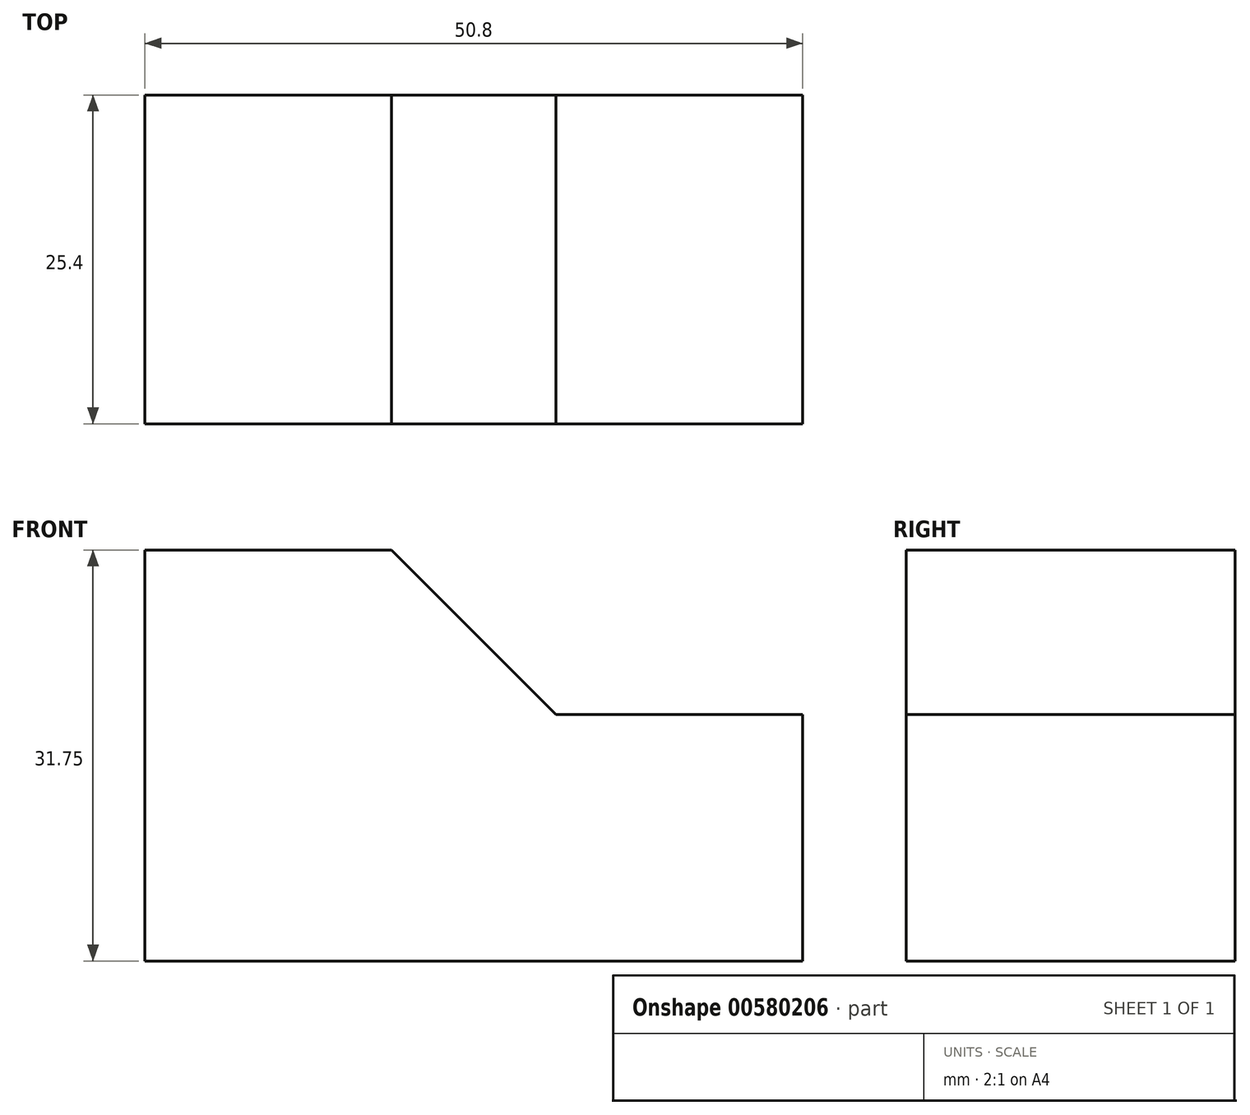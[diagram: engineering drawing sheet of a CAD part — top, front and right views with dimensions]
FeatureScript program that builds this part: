
annotation { "Feature Type Name" : "Feature", "Feature Type Description" : "" }
export const myFeature = defineFeature(function(context is Context, id is Id, definition is map)
    precondition{}
    {
        {
            var Q0;
            Q0=qCreatedBy(makeId("Front.planeOp"),FACE);
            var sketch = newSketch(context, id + "F0", { "sketchPlane" : qUnion([Q0])});
            skLineSegment(sketch, "E0", {"start": v(0, 0) * mm, "end": v(0, 31.75) * mm});
            skLineSegment(sketch, "E1", {"start": v(0, 31.75) * mm, "end": v(19.05, 31.75) * mm});
            skLineSegment(sketch, "E2", {"start": v(19.05, 31.75) * mm, "end": v(50.8, 0) * mm});
            skLineSegment(sketch, "E3", {"start": v(0, 0) * mm, "end": v(50.8, 0) * mm});
            skLineSegment(sketch, "E4", {"start": v(50.8, 0) * mm, "end": v(31.75, 19.05) * mm});
            skLineSegment(sketch, "E5", {"start": v(31.75, 19.05) * mm, "end": v(50.8, 19.05) * mm});
            skLineSegment(sketch, "E6", {"start": v(50.8, 19.05) * mm, "end": v(50.8, 0) * mm});
            skSolve(sketch);
        }
        {
            var Q0;
            Q0 = qSketchRegion(id + "F0", true);
            extrude(context, id + "F1", {"entities" : qUnion([Q0]), "depth" : 25.4 * mm, "offsetDistance" : 25.4 * mm});
        }
    });
